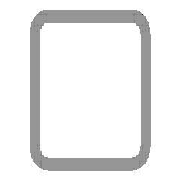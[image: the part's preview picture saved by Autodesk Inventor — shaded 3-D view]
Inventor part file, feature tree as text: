
AUTODESK INVENTOR PART (.ipt)
format: ipt  version: 2021 (Build 250183000, 183)  size: 130,048 bytes
history: native  units: mm (DEFAULTED — no unit token found)
features: other x4, sketch x3, extrude x1, plane x1
ambient origin geometry x8: Origin, YZ Plane, XZ Plane, XY Plane, X Axis, Y Axis, Z Axis, Center Point
bodies: Solid1 (feature_tree)
feature tree (9):
  parser-record x1  (decoder bookkeeping rows leaked as tree rows — omitted from the tree; the rows remain in map.json)
  other  "Driven Length"
  other  "Plano inicial"
  other  "Plano final"
  extrude  "Corpo"  TaperAngle=0.0deg  [1 undecoded]
  sketch  "Esboço"  dims[d11=50.8mm d12=4.7625mm d13=-0.0mm d14=1000.0mm d15=25.4mm d16=25.4mm d17=9.525mm d18=90.0deg d19=1000.0mm]
  sketch  "Sketch3"  dims[d3=1000.0mm d4=0.0mm]
  plane  "Work Plane3"
  sketch  "Sketch4"  dims[d10=50.8mm]
note: 1 required parameter value undecoded (feature->parameter linkage not recoverable at this tier; creation-order binding heuristic only, values carry confidence <= 0.55)
